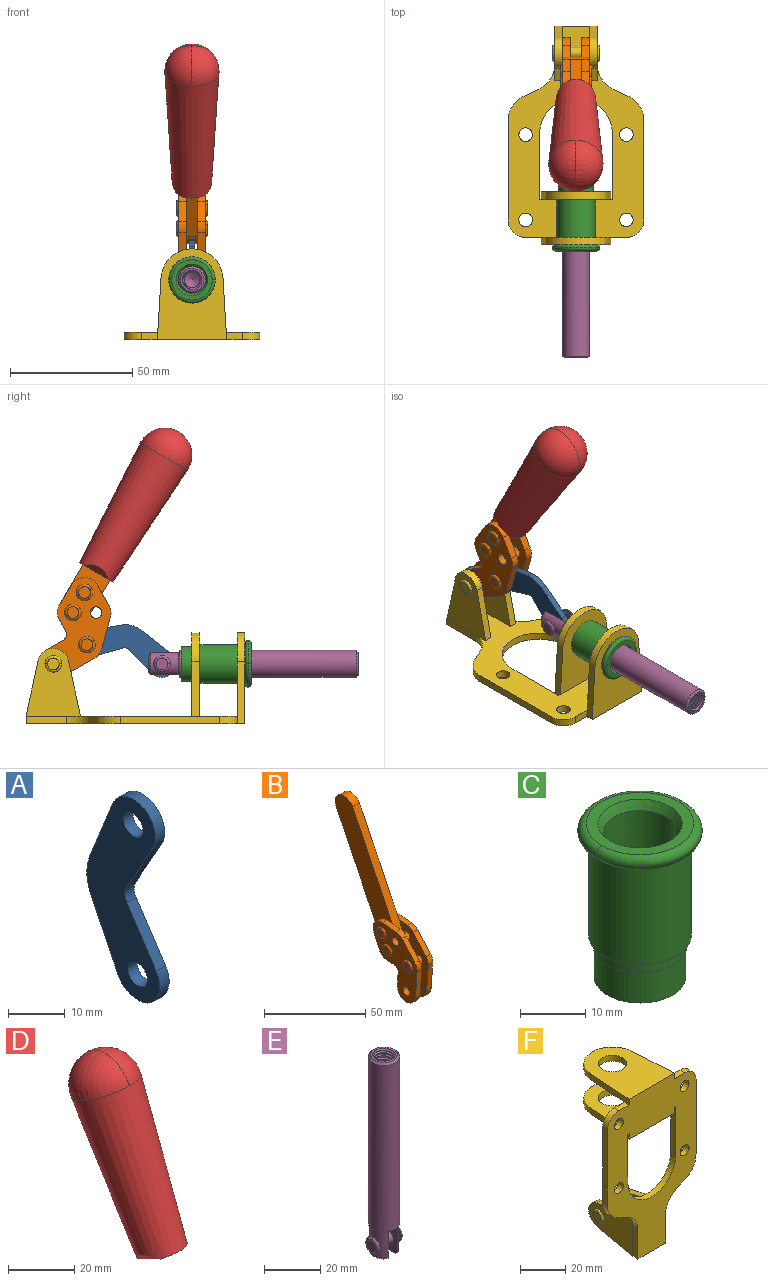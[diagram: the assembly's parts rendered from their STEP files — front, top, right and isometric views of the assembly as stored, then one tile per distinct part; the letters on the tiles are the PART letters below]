
ASSEMBLY  parts=6 mates=6
PART A: 12 faces, bbox 2.3x18.2x42.8 mm
  f0: cylinder r=2.4mm len=4.8mm, axis (1,0,0), area 34.9mm2, adj f4,f11
  f1: cylinder r=10.41mm len=8.47mm, axis (1,0,0), area 20.2mm2, adj f4,f9,f10,f11
  f2: cylinder r=3.05mm len=3.16mm, axis (1,0,0), area 7.7mm2, adj f4,f6,f7,f11
  f3: cylinder r=2.4mm len=4.8mm, axis (1,0,0), area 34.9mm2, adj f4,f11
  f4: plane 42.81x18.23mm, normal (-1,0,0), area 414.1mm2, adj f0,f1,f2,f3,f5,f6,f7,f8
  f5: cylinder r=5.54mm len=10.67mm, axis (1,0,0), area 41.8mm2, adj f4,f6,f10,f11
  f6: plane 11.66x6.53mm, normal (0,-0.87,-0.49), area 30.9mm2, adj f2,f4,f5,f11
  f7: plane 11.17x7.33mm, normal (0,-0.84,0.55), area 30.9mm2, adj f2,f4,f8,f11
  f8: cylinder r=5.54mm len=10.51mm, axis (1,0,0), area 41.8mm2, adj f4,f7,f9,f11
  f9: plane 13.67x6.67mm, normal (0,0.9,-0.44), area 35.1mm2, adj f1,f4,f8,f11
  f10: plane 14.1x5.7mm, normal (0,0.93,0.37), area 35.1mm2, adj f1,f4,f5,f11
  f11: plane 42.81x18.23mm, normal (1,0,0), area 414.1mm2, adj f0,f1,f2,f3,f5,f6,f7,f8
PART B: 59 faces, bbox 12.9x60.2x99.6 mm
  f0: torus R=2.39mm, axis (-1,0,0), area 14.9mm2, adj f20,f43,f51
  f1: torus R=2.39mm, axis (-1,0,0), area 14.9mm2, adj f19,f42,f51
  f2: torus R=2.39mm, axis (-1,0,0), area 14.9mm2, adj f18,f35,f51
  f3: torus R=2.39mm, axis (-1,0,0), area 14.9mm2, adj f14,f17,f23
  f4: torus R=2.39mm, axis (-1,0,0), area 14.9mm2, adj f13,f16,f23
  f5: torus R=2.39mm, axis (-1,0,0), area 14.9mm2, adj f12,f15,f23
  f6: cylinder r=2.39mm len=4.78mm, axis (1,0,0), area 46.5mm2, adj f48,f50,f51
  f7: cylinder r=2.39mm len=4.78mm, axis (1,0,0), area 46.5mm2, adj f50,f51
  f8: cylinder r=6.35mm len=12.68mm, axis (1,0,0), area 61.8mm2, adj f38,f39,f50,f51
  f9: cylinder r=2.39mm len=4.78mm, axis (-1,0,0), area 70.5mm2, adj f46,f50
  f10: cylinder r=2.39mm len=4.78mm, axis (-1,0,0), area 46.5mm2, adj f23,f45,f46
  f11: cylinder r=2.39mm len=4.78mm, axis (-1,0,0), area 46.5mm2, adj f23,f46
  f12: plane 4.78x4.78mm, normal (1,0,0), area 17.9mm2, adj f5,f15
  f13: plane 4.78x4.78mm, normal (1,0,0), area 17.9mm2, adj f4,f16
  f14: plane 4.78x4.78mm, normal (1,0,0), area 17.9mm2, adj f3,f17
  f15: torus R=2.39mm, axis (-1,0,0), area 14.9mm2, adj f5,f12,f23
  f16: torus R=2.39mm, axis (-1,0,0), area 14.9mm2, adj f4,f13,f23
  f17: torus R=2.39mm, axis (-1,0,0), area 14.9mm2, adj f3,f14,f23
  f18: plane 4.78x4.78mm, normal (-1,0,0), area 17.9mm2, adj f2,f35
  f19: plane 4.78x4.78mm, normal (-1,0,0), area 17.9mm2, adj f1,f42
  f20: plane 4.78x4.78mm, normal (-1,0,0), area 17.9mm2, adj f0,f43
  f21: plane 2.26x0.2mm, normal (1,0,0), area 0.2mm2, adj f31,f44
  f22: plane 2.26x0.2mm, normal (-1,0,0), area 0.2mm2, adj f41,f44
  f23: plane 39.37x30.77mm, normal (1,0,0), area 565.5mm2, adj f3,f4,f5,f10,f11,f15,f16,f17
  f24: cylinder r=6.1mm len=4.15mm, axis (-1,0,0), area 14.7mm2, adj f23,f25,f32,f46
  f25: plane 10.25x9.01mm, normal (0,-0.75,0.66), area 42.3mm2, adj f23,f24,f26,f46
  f26: cylinder r=6.35mm len=4.64mm, axis (-1,0,0), area 15.6mm2, adj f23,f25,f27,f46
  f27: plane 15.84x3.1mm, normal (0,-1,-0.07), area 49.2mm2, adj f23,f26,f28,f46
  f28: cylinder r=6.35mm len=12.68mm, axis (-1,0,0), area 61.8mm2, adj f23,f27,f29,f46
  f29: plane 8.11x3.1mm, normal (0,1,0.07), area 25.2mm2, adj f23,f28,f30,f46
  f30: cylinder r=3.05mm len=3.25mm, axis (-1,0,0), area 14.8mm2, adj f23,f29,f31,f46
  f31: plane 5.99x3.1mm, normal (0,0.07,-1), area 18.6mm2, adj f21,f23,f30,f44,f46
  f32: plane 9.5x3.1mm, normal (0,-0.07,1), area 29.5mm2, adj f23,f24,f33,f46,f47
  f33: cylinder r=6.1mm len=8.63mm, axis (-1,0,0), area 39.1mm2, adj f23,f32,f34,f47
  f34: plane 8.65x3.96mm, normal (0,0.91,-0.42), area 29.5mm2, adj f23,f33,f44,f47
  f35: torus R=2.39mm, axis (-1,0,0), area 14.9mm2, adj f2,f18,f51
  f36: plane 10.25x9.01mm, normal (0,-0.75,0.66), area 42.3mm2, adj f37,f49,f50,f51
  f37: cylinder r=6.35mm len=4.64mm, axis (1,0,0), area 15.6mm2, adj f36,f38,f50,f51
  f38: plane 15.84x3.1mm, normal (0,-1,-0.07), area 49.2mm2, adj f8,f37,f50,f51
  f39: plane 8.11x3.1mm, normal (0,1,0.07), area 25.2mm2, adj f8,f40,f50,f51
  f40: cylinder r=3.05mm len=3.25mm, axis (1,0,0), area 14.8mm2, adj f39,f41,f50,f51
  f41: plane 5.99x3.1mm, normal (0,0.07,-1), area 18.6mm2, adj f22,f40,f44,f50,f51
  f42: torus R=2.39mm, axis (-1,0,0), area 14.9mm2, adj f1,f19,f51
  f43: torus R=2.39mm, axis (-1,0,0), area 14.9mm2, adj f0,f20,f51
  f44: cylinder r=6.35mm len=12.12mm, axis (-1,0,0), area 128.9mm2, adj f21,f22,f23,f31,f34,f41,f46,f47
  f45: plane 2.65x1.35mm, normal (1,0,0), area 1mm2, adj f10,f55
  f46: plane 39.08x20.42mm, normal (-1,0,0), area 412.5mm2, adj f9,f10,f11,f24,f25,f26,f27,f28
  f47: plane 77.62x39.82mm, normal (1,0,0), area 850mm2, adj f32,f33,f34,f44,f53,f54,f55
  f48: plane 2.65x1.35mm, normal (-1,0,0), area 1mm2, adj f6,f55
  f49: cylinder r=6.1mm len=4.15mm, axis (1,0,0), area 14.7mm2, adj f36,f50,f51,f56
  f50: plane 39.08x20.42mm, normal (1,0,0), area 412.5mm2, adj f6,f7,f8,f9,f36,f37,f38,f39
  f51: plane 39.37x30.77mm, normal (-1,0,0), area 565.5mm2, adj f0,f1,f2,f6,f7,f8,f35,f36
  f52: plane 8.65x3.96mm, normal (0,0.91,-0.42), area 29.5mm2, adj f44,f51,f57,f58
  f53: plane 68.49x33.4mm, normal (0,0.9,-0.44), area 358.1mm2, adj f44,f47,f54,f58
  f54: cylinder r=6.35mm len=12.06mm, axis (1,0,0), area 93.7mm2, adj f47,f53,f55,f58
  f55: plane 68.49x33.4mm, normal (0,-0.9,0.44), area 358.1mm2, adj f44,f45,f46,f47,f48,f50,f54,f58
  f56: plane 9.5x3.1mm, normal (0,-0.07,1), area 29.5mm2, adj f49,f50,f51,f57,f58
  f57: cylinder r=6.1mm len=8.63mm, axis (1,0,0), area 39.1mm2, adj f51,f52,f56,f58
  f58: plane 77.62x39.82mm, normal (-1,0,0), area 850mm2, adj f44,f52,f53,f54,f55,f56,f57
PART C: 15 faces, bbox 20.6x20.6x28.7 mm
  f0: torus R=8.26mm, axis (0,0,1), area 56.8mm2, adj f1,f10,f12
  f1: torus R=8.26mm, axis (0,0,1), area 56.8mm2, adj f0,f6,f13
  f2: cylinder r=5.59mm len=25.91mm, axis (0,0,1), area 909.6mm2, adj f3,f4
  f3: cone r=6.86mm half-angle=45deg, axis (0,0,-1), area 70.2mm2, adj f2,f14
  f4: cone r=6.47mm half-angle=30deg, axis (0,0,1), area 66.7mm2, adj f2,f13
  f5: cylinder r=7.04mm len=14.07mm, axis (0,0,1), area 252.6mm2, adj f11,f14
  f6: torus R=8.26mm, axis (0,0,1), area 56.8mm2, adj f1,f12,f13
  f7: cylinder r=7.16mm len=14.33mm, axis (0,0,1), area 91.5mm2, adj f9,f11
  f8: cylinder r=7.86mm len=18.42mm, axis (0,0,1), area 909.6mm2, adj f9,f10
  f9: plane 15.72x15.72mm, normal (0,0,-1), area 33mm2, adj f7,f8
  f10: plane 16.51x16.51mm, normal (0,0,-1), area 19.9mm2, adj f0,f8,f12
  f11: plane 14.33x14.33mm, normal (0,0,-1), area 5.7mm2, adj f5,f7
  f12: torus R=8.26mm, axis (0,0,1), area 56.8mm2, adj f0,f6,f10
  f13: plane 16.51x16.51mm, normal (0,0,1), area 82.7mm2, adj f1,f4,f6
  f14: plane 14.07x14.07mm, normal (0,0,-1), area 7.8mm2, adj f3,f5
PART D: 11 faces, bbox 22.3x42.6x64.5 mm
  f0: sphere r=11.13mm, area 411.4mm2, adj f1,f8
  f1: cone r=11.11mm half-angle=3.3deg, axis (0,0.44,0.9), area 3251.8mm2, adj f0,f7,f8,f9,f10
  f2: cylinder r=6.16mm len=11.7mm, axis (1,0,0), area 89.5mm2, adj f3,f4,f5,f6
  f3: plane 60.23x36.75mm, normal (-1,0,0), area 763.6mm2, adj f2,f4,f6,f10
  f4: plane 51.37x25.05mm, normal (0,0.9,-0.44), area 264.2mm2, adj f2,f3,f5,f10
  f5: plane 60.23x36.75mm, normal (1,0,0), area 763.6mm2, adj f2,f4,f6,f10
  f6: plane 51.37x25.05mm, normal (0,-0.9,0.44), area 264.2mm2, adj f2,f3,f5,f10
  f7: plane 9.95x5.95mm, normal (0.71,-0.31,-0.64), area 25.8mm2, adj f1,f10
  f8: sphere r=11.13mm, area 411.4mm2, adj f0,f1
  f9: plane 9.95x5.95mm, normal (-0.71,-0.31,-0.64), area 25.8mm2, adj f1,f10
  f10: plane 14.27x11.38mm, normal (0,-0.44,-0.9), area 106.7mm2, adj f1,f3,f4,f5,f6,f7,f9
PART E: 48 faces, bbox 12.6x11.1x86.1 mm
  f0: torus R=2.41mm, axis (-1,0,0), area 15mm2, adj f30,f32,f34
  f1: torus R=2.41mm, axis (-1,0,0), area 15mm2, adj f29,f31,f33
  f2: cylinder r=5.54mm len=72.39mm, axis (0,0,1), area 2518.5mm2, adj f3,f4,f42,f43
  f3: cone r=5.54mm half-angle=45deg, axis (0,0,1), area 7.6mm2, adj f2,f5,f41
  f4: cone r=5.54mm half-angle=45deg, axis (0,0,-1), area 34.9mm2, adj f2,f39
  f5: cylinder r=5.08mm len=11.48mm, axis (0,0,1), area 108.3mm2, adj f3,f7,f8,f41
  f6: cylinder r=2.41mm len=4.83mm, axis (-1,0,0), area 71.2mm2, adj f40,f41
  f7: cylinder r=2.41mm len=4.83mm, axis (-1,0,0), area 7.6mm2, adj f5,f34
  f8: cone r=5.08mm half-angle=45deg, axis (0,0,1), area 10.6mm2, adj f5,f37,f41
  f9: cone r=3.98mm half-angle=45deg, axis (0,0,1), area 17.6mm2, adj f27,f39,f45,f46,f47
  f10: cylinder r=2.41mm len=4.83mm, axis (-1,0,0), area 7.6mm2, adj f33,f38
  f11: cylinder r=3.2mm len=6.4mm, axis (0,0,1), area 78.4mm2, adj f12,f28,f44,f45,f47
  f12: cylinder r=3.2mm len=6.4mm, axis (0,0,1), area 10.5mm2, adj f11,f13,f45,f47
  f13: cylinder r=3.2mm len=6.4mm, axis (0,0,1), area 10.5mm2, adj f12,f14,f45,f47
  f14: cylinder r=3.2mm len=6.4mm, axis (0,0,1), area 10.5mm2, adj f13,f15,f45,f47
  f15: cylinder r=3.2mm len=6.4mm, axis (0,0,1), area 10.5mm2, adj f14,f16,f45,f47
  f16: cylinder r=3.2mm len=6.4mm, axis (0,0,1), area 10.5mm2, adj f15,f17,f45,f47
  f17: cylinder r=3.2mm len=6.4mm, axis (0,0,1), area 10.5mm2, adj f16,f18,f45,f47
  f18: cylinder r=3.2mm len=6.4mm, axis (0,0,1), area 10.5mm2, adj f17,f19,f45,f47
  f19: cylinder r=3.2mm len=6.4mm, axis (0,0,1), area 10.5mm2, adj f18,f20,f45,f47
  f20: cylinder r=3.2mm len=6.4mm, axis (0,0,1), area 10.5mm2, adj f19,f21,f45,f47
  f21: cylinder r=3.2mm len=6.4mm, axis (0,0,1), area 10.5mm2, adj f20,f22,f45,f47
  f22: cylinder r=3.2mm len=6.4mm, axis (0,0,1), area 10.5mm2, adj f21,f23,f45,f47
  f23: cylinder r=3.2mm len=6.4mm, axis (0,0,1), area 10.5mm2, adj f22,f24,f45,f47
  f24: cylinder r=3.2mm len=6.4mm, axis (0,0,1), area 10.5mm2, adj f23,f25,f45,f47
  f25: cylinder r=3.2mm len=6.4mm, axis (0,0,1), area 10.5mm2, adj f24,f26,f45,f47
  f26: cylinder r=3.2mm len=6.4mm, axis (0,0,1), area 10.5mm2, adj f25,f27,f45,f47
  f27: cylinder r=3.2mm len=6.4mm, axis (0,0,1), area 7.4mm2, adj f9,f26,f45,f47
  f28: cone r=3.2mm half-angle=60deg, axis (0,0,1), area 37.2mm2, adj f11
  f29: plane 4.83x4.83mm, normal (-1,0,0), area 18.3mm2, adj f1,f31
  f30: plane 4.83x4.83mm, normal (1,0,0), area 18.3mm2, adj f0,f32
  f31: torus R=2.41mm, axis (-1,0,0), area 15mm2, adj f1,f29,f33
  f32: torus R=2.41mm, axis (-1,0,0), area 15mm2, adj f0,f30,f34
  f33: plane 6.83x6.83mm, normal (1,0,0), area 18.3mm2, adj f1,f10,f31
  f34: plane 6.83x6.83mm, normal (-1,0,0), area 18.3mm2, adj f0,f7,f32
  f35: cone r=5.08mm half-angle=45deg, axis (0,0,1), area 10.6mm2, adj f36,f38,f40
  f36: plane 7.25x1.97mm, normal (0,0,-1), area 10mm2, adj f35,f40
  f37: plane 7.25x1.97mm, normal (0,0,-1), area 10mm2, adj f8,f41
  f38: cylinder r=5.08mm len=11.48mm, axis (0,0,1), area 108.3mm2, adj f10,f35,f40,f42
  f39: plane 9.55x9.55mm, normal (0,0,1), area 22mm2, adj f4,f9
  f40: plane 12.76x10.09mm, normal (1,0,0), area 95.7mm2, adj f6,f35,f36,f38,f42,f43
  f41: plane 12.76x10.09mm, normal (-1,0,0), area 95.7mm2, adj f3,f5,f6,f8,f37,f43
  f42: cone r=5.54mm half-angle=45deg, axis (0,0,1), area 7.6mm2, adj f2,f38,f40
  f43: plane 11.07x4.7mm, normal (0,0,-1), area 50.4mm2, adj f2,f40,f41
  f44: plane 0.89x0.62mm, normal (-1,0,0), area 0.3mm2, adj f11,f45,f46,f47
  f45: bspline ~24.8x7.63mm, area 266.6mm2, adj f9,f11,f12,f13,f14,f15,f16,f17
  f46: bspline ~24.87x7.63mm, area 73.6mm2, adj f9,f44,f45,f47
  f47: bspline ~24.98x7.63mm, area 272.5mm2, adj f9,f11,f12,f13,f14,f15,f16,f17
PART F: 55 faces, bbox 55.7x37.4x89.8 mm
  f0: torus R=2.41mm, axis (-1,0,0), area 15mm2, adj f11,f15,f25
  f1: torus R=2.41mm, axis (-1,0,0), area 15mm2, adj f10,f12,f22
  f2: cylinder r=2.78mm len=5.56mm, axis (0,-1,0), area 54.2mm2, adj f30,f54
  f3: cylinder r=14.99mm len=29.97mm, axis (0,-1,0), area 145.9mm2, adj f30,f49,f53,f54
  f4: cylinder r=2.78mm len=5.56mm, axis (0,-1,0), area 54.2mm2, adj f30,f54
  f5: cylinder r=2.78mm len=5.56mm, axis (0,-1,0), area 54.2mm2, adj f30,f54
  f6: cylinder r=2.78mm len=5.56mm, axis (0,-1,0), area 54.2mm2, adj f30,f54
  f7: cylinder r=6.35mm len=12.7mm, axis (0,0,1), area 123.6mm2, adj f27,f51
  f8: cylinder r=6.35mm len=12.7mm, axis (0,0,-1), area 124.7mm2, adj f21,f35
  f9: cylinder r=2.41mm len=11.18mm, axis (-1,0,0), area 169.4mm2, adj f16,f19
  f10: plane 4.83x4.83mm, normal (1,0,0), area 18.3mm2, adj f1,f12
  f11: plane 4.83x4.83mm, normal (-1,0,0), area 18.3mm2, adj f0,f15
  f12: torus R=2.41mm, axis (-1,0,0), area 15mm2, adj f1,f10,f22
  f13: cylinder r=6.35mm len=12.41mm, axis (1,0,0), area 53.4mm2, adj f18,f19,f22,f23
  f14: cylinder r=6.35mm len=12.41mm, axis (-1,0,0), area 53.4mm2, adj f16,f17,f24,f25
  f15: torus R=2.41mm, axis (-1,0,0), area 15mm2, adj f0,f11,f25
  f16: plane 27.86x22.35mm, normal (1,0,0), area 425.4mm2, adj f9,f14,f17,f24,f30
  f17: plane 22.86x4.97mm, normal (0,0.21,0.98), area 72.5mm2, adj f14,f16,f25,f30
  f18: plane 22.86x4.97mm, normal (0,0.21,0.98), area 72.5mm2, adj f13,f19,f22,f30
  f19: plane 27.86x22.35mm, normal (-1,0,0), area 425.4mm2, adj f9,f13,f18,f23,f30
  f20: cylinder r=12.7mm len=25.35mm, axis (0,0,-1), area 119.8mm2, adj f21,f34,f35,f36
  f21: plane 34.21x28.07mm, normal (0,0,-1), area 702.4mm2, adj f8,f20,f30,f34,f36
  f22: plane 27.96x22.45mm, normal (1,0,0), area 407.2mm2, adj f1,f12,f13,f18,f23,f30,f42,f43
  f23: plane 22.86x4.97mm, normal (0,0.21,-0.98), area 72.5mm2, adj f13,f19,f22,f44
  f24: plane 22.86x4.97mm, normal (0,0.21,-0.98), area 72.5mm2, adj f14,f16,f25,f44
  f25: plane 27.86x22.35mm, normal (-1,0,0), area 407.1mm2, adj f0,f14,f15,f17,f24,f30,f45,f46
  f26: plane 3.1x0.95mm, normal (0,0,-1), area 2.7mm2, adj f30,f49,f50,f54
  f27: plane 34.21x28.07mm, normal (0,0,1), area 702.4mm2, adj f7,f28,f30,f50,f52
  f28: cylinder r=12.7mm len=25.35mm, axis (0,0,1), area 118.8mm2, adj f27,f50,f51,f52
  f29: plane 3.1x0.95mm, normal (0,0,-1), area 2.7mm2, adj f30,f52,f53,f54
  f30: plane 86.54x55.63mm, normal (0,1,0), area 2362.9mm2, adj f2,f3,f4,f5,f6,f16,f17,f18
  f31: plane 40.56x3.1mm, normal (-1,0,0), area 125.7mm2, adj f30,f32,f48,f54
  f32: cylinder r=7.11mm len=7.11mm, axis (0,-1,0), area 34.6mm2, adj f30,f31,f33,f54
  f33: plane 6.67x3.1mm, normal (0,0,1), area 20.4mm2, adj f30,f32,f34,f54
  f34: plane 25.39x3.13mm, normal (-1,0.06,0), area 79.5mm2, adj f20,f21,f33,f35,f54
  f35: plane 37.31x28.45mm, normal (0,0,1), area 789.9mm2, adj f8,f20,f34,f36,f54
  f36: plane 25.39x3.13mm, normal (1,0.06,0), area 79.5mm2, adj f20,f21,f35,f37,f54
  f37: plane 6.67x3.1mm, normal (0,0,1), area 20.4mm2, adj f30,f36,f38,f54
  f38: cylinder r=7.11mm len=7.11mm, axis (0,-1,0), area 34.6mm2, adj f30,f37,f39,f54
  f39: plane 40.56x3.1mm, normal (1,0,0), area 125.7mm2, adj f30,f38,f40,f54
  f40: cylinder r=11.18mm len=10.16mm, axis (0,-1,0), area 39.5mm2, adj f30,f39,f41,f54
  f41: plane 6.09x3.1mm, normal (0.42,0,-0.91), area 20.8mm2, adj f30,f40,f42,f54
  f42: cylinder r=11.18mm len=9.41mm, axis (0,-1,0), area 37.2mm2, adj f22,f30,f41,f43,f54
  f43: plane 16.5x3.1mm, normal (1,0,0), area 51.1mm2, adj f22,f42,f44,f54
  f44: plane 17.37x3.1mm, normal (0,0,-1), area 53.8mm2, adj f23,f24,f30,f43,f45,f54
  f45: plane 16.5x3.1mm, normal (-1,0,0), area 51.1mm2, adj f25,f44,f46,f54
  f46: cylinder r=11.18mm len=9.41mm, axis (0,-1,0), area 37.2mm2, adj f25,f30,f45,f47,f54
  f47: plane 6.09x3.1mm, normal (-0.42,0,-0.91), area 20.8mm2, adj f30,f46,f48,f54
  f48: cylinder r=11.18mm len=10.16mm, axis (0,-1,0), area 39.5mm2, adj f30,f31,f47,f54
  f49: plane 26.54x3.1mm, normal (-1,0,0), area 82.3mm2, adj f3,f26,f30,f54
  f50: plane 25.39x3.1mm, normal (1,0.06,0), area 78.8mm2, adj f26,f27,f28,f51,f54
  f51: plane 37.31x28.45mm, normal (0,0,-1), area 789.9mm2, adj f7,f28,f50,f52,f54
  f52: plane 25.39x3.1mm, normal (-1,0.06,0), area 78.8mm2, adj f27,f28,f29,f51,f54
  f53: plane 26.54x3.1mm, normal (1,0,0), area 82.3mm2, adj f3,f29,f30,f54
  f54: plane 89.66x55.63mm, normal (0,-1,0), area 2678.5mm2, adj f2,f3,f4,f5,f6,f26,f29,f31
PLACE A rot(axis=(0,-0.63,-0.78),180deg) t=(0,17.6,5.13)mm
PLACE B rot(axis=(1,0,0),56.3deg) t=(0,0.87,21.97)mm
PLACE C rot(axis=(1,0,0),90deg) t=(0,9.14,0)mm
PLACE D rot(axis=(1,0,0),56.3deg) t=(-0.04,0.87,21.97)mm
PLACE E rot(axis=(1,0,0),90deg) t=(0,12.17,0)mm
PLACE F rot(axis=(1,0,0),90deg) t=(0,9.14,0)mm fixed
MATE revolute A.f3 <-> E.f6  axis (-1,0,0) through (0,-3.31,24.61)mm
MATE fastened C.f2 <-> F.f7  axis (0,-1,0) through (0,-37.25,24.61)mm
MATE slider E.f2 <-> F.f7  axis (0,-1,0) through (0,-46.62,24.61)mm
MATE revolute A.f5 <-> B.f4  axis (-1,0,0) through (0,27.45,32.49)mm
MATE fastened D.f2 <-> B.f54  axis (1,0,0) through (-2.35,-5.21,111.47)mm
MATE revolute B.f7 <-> F.f0  axis (1,0,0) through (0,41.23,24.61)mm
